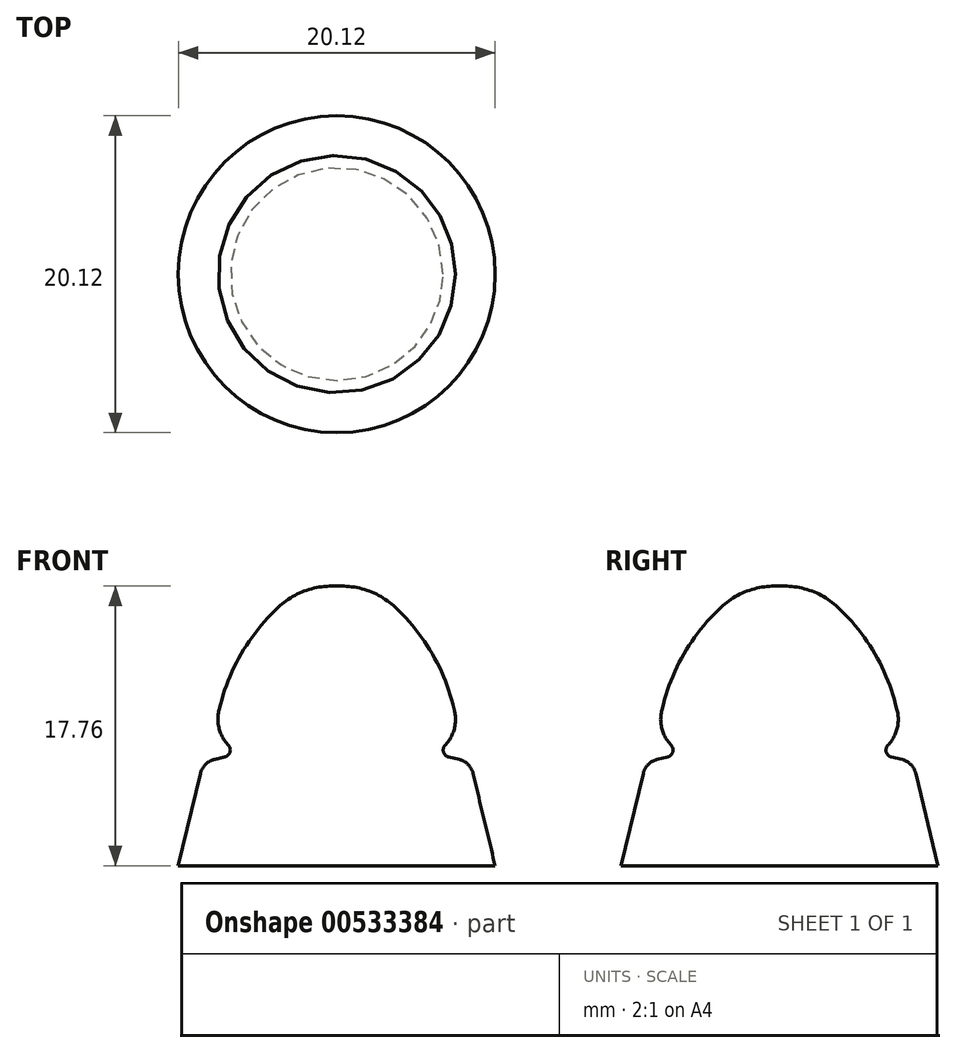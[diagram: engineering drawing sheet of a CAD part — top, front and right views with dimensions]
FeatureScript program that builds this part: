
annotation { "Feature Type Name" : "Feature", "Feature Type Description" : "" }
export const myFeature = defineFeature(function(context is Context, id is Id, definition is map)
    precondition{}
    {
        {
            var Q0;
            Q0=qCreatedBy(makeId("Front.planeOp"),FACE);
            var sketch = newSketch(context, id + "F0", { "sketchPlane" : qUnion([Q0])});
            skLineSegment(sketch, "E0", {"start": v(0, 0) * mm, "end": v(-10.06, 0) * mm});
            skLineSegment(sketch, "E1", {"start": v(-10.06, 0) * mm, "end": v(-8.49, 6.56) * mm});
            skLineSegment(sketch, "E2", {"start": v(-8.49, 6.56) * mm, "end": v(-6.39, 7.09) * mm});
            skLineSegment(sketch, "E3", {"start": v(-6.39, 7.09) * mm, "end": v(-7.79, 8.66) * mm});
            skLineSegment(sketch, "E4", {"start": v(-7.79, 8.66) * mm, "end": v(-6.39, 14.09) * mm});
            skLineSegment(sketch, "E5", {"start": v(-6.39, 14.09) * mm, "end": v(-2.19, 17.76) * mm});
            skLineSegment(sketch, "E6", {"start": v(-2.19, 17.76) * mm, "end": v(0, 17.76) * mm});
            skLineSegment(sketch, "E7", {"start": v(0, 17.76) * mm, "end": v(0, 0) * mm});
            skSolve(sketch);
        }
        {
            var Q0;
            Q0=makeQuery(id+"F0.imprint","IMPRINT",FACE,{"disambiguationData":[TD([[makeQuery(id+"F0.imprint","IMPRINT",EDGE,{"derivedFrom":sQuery(id+"F0.wireOp",EDGE,"E0")}),-1.0]])]});
            var Q1;
            Q1=sQuery(id+"F0.wireOp",EDGE,"E7");
            revolve(context, id + "F1", {"entities" : qUnion([Q0]), "axis" : qUnion([Q1]), "revolveType" : RevolveType.FULL});
        }
        {
            var Q0;
            Q0=makeQuery(id+"F1.opRevolve","SWEPT_EDGE",EDGE,{"disambiguationData":[OSD([sQuery(id+"F0.wireOp",EDGE,"E4"),sQuery(id+"F0.wireOp",EDGE,"E5")])]});
            fillet(context, id + "F2", {"entities" : qUnion([Q0]), "radius" : 12.86 * mm, "tangentPropagation" : true, "allowEdgeOverflow" : false});
        }
        {
            var Q0;
            Q0=makeQuery(id+"F1.opRevolve","SWEPT_EDGE",EDGE,{"disambiguationData":[OSD([sQuery(id+"F0.wireOp",EDGE,"E1"),sQuery(id+"F0.wireOp",EDGE,"E2")])]});
            fillet(context, id + "F3", {"entities" : qUnion([Q0]), "radius" : 1.18 * mm, "tangentPropagation" : true, "allowEdgeOverflow" : false});
        }
        {
            var Q0;
            Q0=makeQuery(id+"F1.opRevolve","SWEPT_EDGE",EDGE,{"disambiguationData":[OSD([sQuery(id+"F0.wireOp",EDGE,"E3"),sQuery(id+"F0.wireOp",EDGE,"E4")])]});
            fillet(context, id + "F4", {"entities" : qUnion([Q0]), "radius" : 2.4 * mm, "tangentPropagation" : true, "allowEdgeOverflow" : false});
        }
        {
            var Q0;
            Q0=makeQuery(id+"F1.opRevolve","SWEPT_FACE",FACE,{"disambiguationData":[OSD([sQuery(id+"F0.wireOp",EDGE,"E3")])]});
            fillet(context, id + "F5", {"entities" : qUnion([Q0]), "radius" : 0.44 * mm, "tangentPropagation" : true, "allowEdgeOverflow" : false});
        }
        {
            var Q0;
            Q0=makeQuery(id+"F1.opRevolve","SWEPT_FACE",FACE,{"disambiguationData":[OSD([sQuery(id+"F0.wireOp",EDGE,"E5")])]});
            fillet(context, id + "F6", {"entities" : qUnion([Q0]), "radius" : 5 * mm, "tangentPropagation" : true, "allowEdgeOverflow" : false});
        }
    });
